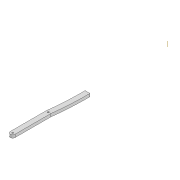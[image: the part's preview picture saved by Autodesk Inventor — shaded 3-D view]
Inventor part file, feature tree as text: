
AUTODESK INVENTOR PART (.ipt)
format: ipt  version: 2022 (Build 260153000, 153)  size: 108,032 bytes
history: native  units: mm
features: extrude x2, sketch x2, other x1
ambient origin geometry x8: Origin, YZ Plane, XZ Plane, XY Plane, X Axis, Y Axis, Z Axis, Center Point
bodies: Solid1 (feature_tree)
feature tree (5):
  extrude  "Extrusion1"  Depth=3.3mm
  other  "Work Axis3"
  extrude  "Extrusion2"  Depth=600.0mm
  sketch  "Sketch1"  dims[d0=3.3mm d1=3.3mm]
  sketch  "Sketch2"  dims[d2=10.0mm d3=322.934mm d4=3.3mm d5=74.182mm d6=6.0mm d7=0.0mm d8=3.3mm d9=218.733mm d12=600.0mm d13=600.0mm d14=100.0mm d15=0.0mm]
